# Revit family: Lighting-StreetLighting-GEWISS-STREET[O3]-LED_OPTIC_CYCLE-PEDESTRIAN
name_source: partatom
category: Apparecchi per illuminazione
units: mm (PartAtom-declared; Revit-internal decimal feet)

## family parameters
Basato su piano di lavoro = No
Condiviso = No
Numero OmniClass = 23.80.70.00
Punto di calcolo locali = No
Quota connettore circolare = Usa diametro
Sempre verticale = Sì
Sorgente d'illuminazione = No
Taglio con vuoti quando caricato = No
Tipo di parte = Normale
Titolo OmniClass = Lighting

## types (6) — shared parameters
Altezza da terra testa staffa = 822 mm
Application = External
Carico apparente = 68 VA
Catalogue = LIGHTING
Catalogue Range = STREET [O3]
Colour = Graphite/Aluminium
Commenti sul wattaggio = 68W
IDF = 0fe26560-d2f1-4d96-bd76-f87854a9d7be
IDT = fe79b716-81a6-4571-bc62-3b977ad29964
IP degree = IP66
Immagine tipo = GWS7001.jpg
Insulation class = II
LED LifeTime (L80B20) = 50000H
LED current = 700 mA
L_staffa = 120 mm  [stored 0.393701 ft]
Lamp = LED
Lampada = LED
Maximum surface exposed to the wind = 0,26M2
Minimum distance from the illuminated object = 1M
Numero di poli = 2
Optic = Cycle and pedestrian - ULOR: 0%
Photobiologic Risk = RG1/RG2 @ 20cm
Produttore = GEWISS S.p.A.
SEO = Street lighting
Shock resistance = IK08 BODY - IK06 LENS
Struttura = <Per categoria>
Technical sheet = https://www.gewiss.com
Tilt adjustable = ±20° bracket - 0°÷20° pole head
URL = https://www.gewiss.com
Version file RFA = 20.11
Vetro = GEWISS - Led - lm 650 / Temp_3000_K
Voltage: = 220/240 V - 50/60 Hz
Voltaggio = 230 V
Warranty = 5 years

## per-type parameters (varying)
| type | Colour temperature | Colour temperature: | Descrizione | Driver type | EAN code | Electrocod | LED Life time (L80B10) | LED Life time (L90B20) | Lumen output (lm) | Material | Modello | No. Chorus modules | Nominal flux (lm) | Number of modules | Operating temperature: | Risk photobiological | System power | Typology | Voltage | Weight (kg) | Weight (kg): | Working temperature |
| GWS7110 - STREET LED 1M 4000K 700mA CYCLE | 4000 K (CRI 70) | 4000 K (CRI 70) | STREET LED 1M 4000K 700mA CYCLE | Constant Current Driver Led | 8011564804807 | 244C | 100000H | 50000H | 3260 | Die-cast  aluminium | GWS7110 | 1 (1x16 LED) | 4140 | 1 (1x16 LED) | -25 +50 °C | RG1/RG2 @ 20cm | 37W | Stand alone | 220/240 V - 50/60 Hz - Stand alone and/or possibility of dimmer 1-10 V | 8,5 | 8,5 | -25 +25 °C |
| GWS7111V - STREET LED 2M 4000K 700mA CYCLE |  | 4000 K (CRI>70) | STREET LED 2M 4000K 700mA CYCLE |  |  | 244C |  |  | 6330 |  | GWS7111V |  | 8050 | 2 (2x16 LED) | -25 +25 °C |  | 68W | Programmable (5 step) | 220/240 V - 50/60 Hz - Stand alone and/or programmable |  | 9,09999999999999 |  |
| GWS7112 - STREET LED 3M 4000K 700mA CYCLE | 4000 K (CRI 70) | 4000 K (CRI 70) | STREET LED 3M 4000K 700mA CYCLE | Constant Current Driver Led | 8011564804920 | 244B | 100000H | 50000H | 9250 | Die-cast  aluminium | GWS7112 | 3 (3x16 LED) | 11740 | 3 (3x16 LED) | -25 +40 °C | RG1/RG2 @ 20cm | 99W | Stand alone | 220/240 V - 50/60 Hz - Stand alone and/or possibility of dimmer 1-10 V | 9,6 | 9,6 | -25 +25 °C |
| GWS7110V - STREET LED 1M 4000K 700mA CYCLE |  | 4000 K (CRI>70) | STREET LED 1M 4000K 700mA CYCLE |  |  | 244C |  |  | 3260 |  | GWS7110V |  | 4140 | 1 (1x16 LED) | -25 +25 °C |  | 37W | Programmable (5 step) | 220/240 V - 50/60 Hz - Stand alone and/or programmable |  | 8,5 |  |
| GWS7112V - STREET LED 3M 4000K 700mA CYCLE |  | 4000 K (CRI>70) | STREET LED 3M 4000K 700mA CYCLE |  |  | 244B |  |  | 9250 |  | GWS7112V |  | 11740 | 3 (3x16 LED) | -25 +25 °C |  | 99W | Programmable (5 step) | 220/240 V - 50/60 Hz - Stand alone and/or programmable |  | 9,59999999999999 |  |
| GWS7111 - STREET LED 2M 4000K 700mA CYCLE | 4000 K (CRI 70) | 4000 K (CRI 70) | STREET LED 2M 4000K 700mA CYCLE | Constant Current Driver Led | 8011564804913 | 244C | 100000H | 50000H | 6330 | Die-cast  aluminium | GWS7111 | 2 (2x16 LED) | 8050 | 2 (2x16 LED) | -25 +35 °C | RG1/RG2 @ 20cm | 68W | Stand alone | 220/240 V - 50/60 Hz - Stand alone and/or possibility of dimmer 1-10 V | 9,1 | 9,1 | -25 +25 °C |

note: [stored X ft] marks values corroborated as IEEE doubles in the binary element streams (Revit-internal decimal feet)
